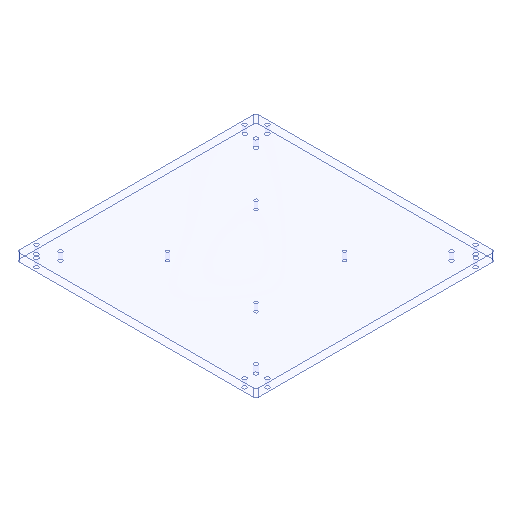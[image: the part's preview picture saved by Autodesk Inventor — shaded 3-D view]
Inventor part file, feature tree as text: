
AUTODESK INVENTOR PART (.ipt)
format: ipt  version: 2023 (Build 270158000, 158)  size: 148,480 bytes
history: native  units: mm
features: extrude x2, sketch x2, other x1
ambient origin geometry x8: Origin, YZ Plane, XZ Plane, XY Plane, X Axis, Y Axis, Z Axis, Center Point
bodies: Solid1 (feature_tree)
feature tree (5):
  extrude  "Extrusion1"  Depth=148.5mm
  extrude  "Extrusion2"  Depth=10.0mm
  sketch  "Sketch2"  dims[d2=148.5mm d3=148.5mm]
  sketch  "Sketch3"  dims[d4=110.0mm d5=110.0mm d6=4.0mm d7=4.0mm d8=4.0mm d9=4.0mm d10=10.0mm d11=0.0mm d12=10.0mm d13=0.0mm]
  other  "Cut-Extrude14"
